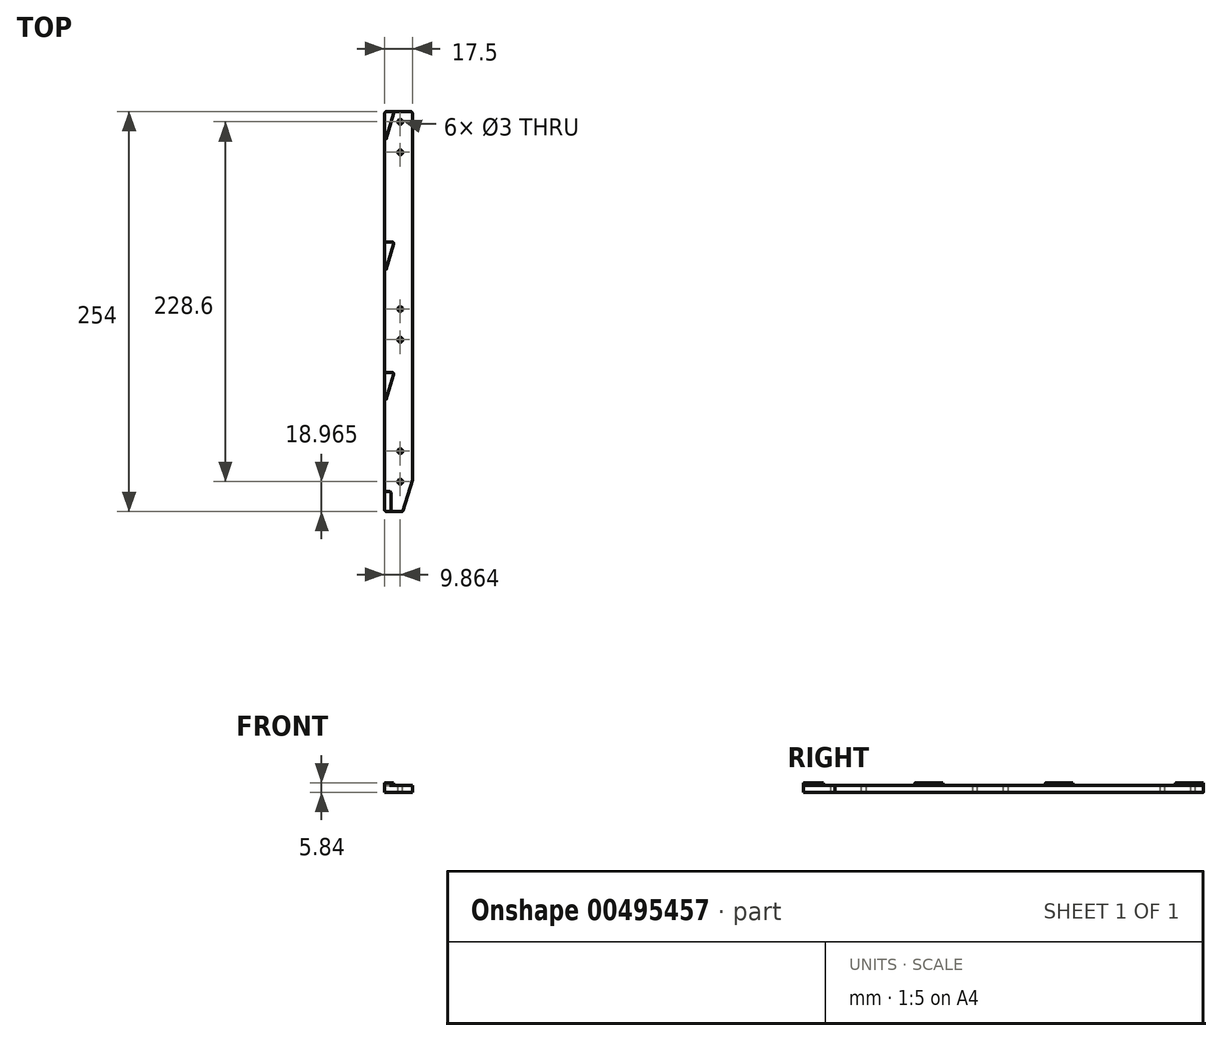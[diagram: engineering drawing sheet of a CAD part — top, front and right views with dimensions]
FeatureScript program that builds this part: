
annotation { "Feature Type Name" : "Feature", "Feature Type Description" : "" }
export const myFeature = defineFeature(function(context is Context, id is Id, definition is map)
    precondition{}
    {
        {
            var Q0;
            Q0=qCreatedBy(makeId("Top.planeOp"),FACE);
            var sketch = newSketch(context, id + "F0", { "sketchPlane" : qUnion([Q0])});
            skLineSegment(sketch, "E0.bottom", {"start": v(-8.75, 106.97) * mm, "end": v(8.75, 106.97) * mm});
            skLineSegment(sketch, "E0.top", {"start": v(-8.75, -147.03) * mm, "end": v(2.75, -147.03) * mm});
            skLineSegment(sketch, "E0.left", {"start": v(-8.75, 106.97) * mm, "end": v(-8.75, -147.03) * mm});
            skLineSegment(sketch, "E0.right", {"start": v(8.75, 106.97) * mm, "end": v(8.75, -127.03) * mm});
            skLineSegment(sketch, "E1", {"start": v(-6.3, -147.03) * mm, "end": v(23.25, -147.03) * mm, "construction": true});
            skLineSegment(sketch, "E2", {"start": v(23.25, -147.03) * mm, "end": v(23.25, -146.28) * mm, "construction": true});
            skLineSegment(sketch, "E3", {"start": v(2.75, -147.03) * mm, "end": v(8.75, -127.03) * mm});
            skLineSegment(sketch, "E4", {"start": v(8.75, -127.03) * mm, "end": v(8.75, -150.96) * mm, "construction": true});
            skSolve(sketch);
        }
        {
            var Q0;
            Q0 = qSketchRegion(id + "F0", true);
            extrude(context, id + "F1", {"entities" : qUnion([Q0]), "oppositeDirection" : true, "depth" : 4.25 * mm});
        }
        {
            var Q0;
            Q0=makeQuery(id+"F1.opExtrude","CAP_FACE",FACE,{"disambiguationData":[OSD([sQuery(id+"F0.wireOp",EDGE,"E0.bottom"),sQuery(id+"F0.wireOp",EDGE,"E0.top"),sQuery(id+"F0.wireOp",EDGE,"E0.left"),sQuery(id+"F0.wireOp",EDGE,"E0.right")])],"isStart":true});
            var sketch = newSketch(context, id + "F2", { "sketchPlane" : qUnion([Q0])});
            skLineSegment(sketch, "E5", {"start": v(-8.75, 106.97) * mm, "end": v(-2.75, 106.97) * mm});
            skLineSegment(sketch, "E6", {"start": v(-2.75, 106.97) * mm, "end": v(-8.75, 86.97) * mm});
            skLineSegment(sketch, "E7", {"start": v(-8.75, 86.97) * mm, "end": v(-8.75, 106.97) * mm});
            skLineSegment(sketch, "E8", {"start": v(-8.75, 24.19) * mm, "end": v(-2.75, 24.19) * mm});
            skLineSegment(sketch, "E9", {"start": v(-2.75, 24.19) * mm, "end": v(-8.75, 4.19) * mm});
            skLineSegment(sketch, "E10", {"start": v(-8.75, 4.19) * mm, "end": v(-8.75, 24.19) * mm});
            skLineSegment(sketch, "E11", {"start": v(-8.75, -58.6) * mm, "end": v(-2.75, -58.6) * mm});
            skLineSegment(sketch, "E12", {"start": v(-2.75, -58.6) * mm, "end": v(-8.75, -78.6) * mm});
            skLineSegment(sketch, "E13", {"start": v(-8.75, -78.6) * mm, "end": v(-8.75, -58.6) * mm});
            skLineSegment(sketch, "E14", {"start": v(-8.75, -134.33) * mm, "end": v(-4.75, -134.33) * mm});
            skLineSegment(sketch, "E15", {"start": v(-4.75, -134.33) * mm, "end": v(-4.75, -147.03) * mm});
            skLineSegment(sketch, "E16", {"start": v(-4.75, -147.03) * mm, "end": v(-8.75, -147.03) * mm});
            skLineSegment(sketch, "E17", {"start": v(-8.75, -147.03) * mm, "end": v(-8.75, -134.33) * mm});
            skSolve(sketch);
        }
        {
            var Q0;
            Q0=makeQuery(id+"F2.imprint","IMPRINT",FACE,{"disambiguationData":[TD([[makeQuery(id+"F2.imprint","IMPRINT",EDGE,{"derivedFrom":sQuery(id+"F2.wireOp",EDGE,"E8")}),-1.0]])]});
            var Q1;
            Q1=makeQuery(id+"F2.imprint","IMPRINT",FACE,{"disambiguationData":[TD([[makeQuery(id+"F2.imprint","IMPRINT",EDGE,{"derivedFrom":sQuery(id+"F2.wireOp",EDGE,"E11")}),-1.0]])]});
            var Q2;
            Q2=makeQuery(id+"F2.imprint","IMPRINT",FACE,{"disambiguationData":[TD([[makeQuery(id+"F2.imprint","IMPRINT",EDGE,{"derivedFrom":sQuery(id+"F2.wireOp",EDGE,"E14")}),-1.0]])]});
            var Q3;
            Q3=makeQuery(id+"F2.imprint","IMPRINT",FACE,{"disambiguationData":[TD([[makeQuery(id+"F2.imprint","IMPRINT",EDGE,{"derivedFrom":sQuery(id+"F2.wireOp",EDGE,"E5")}),-1.0]])]});
            extrude(context, id + "F3", {"entities" : qUnion([Q0, Q1, Q2, Q3]), "operationType" : NewBodyOperationType.ADD, "depth" : 1.59 * mm});
        }
        {
            var Q0;
            Q0=makeQuery(id+"F3.opExtrude","SWEPT_EDGE",EDGE,{"disambiguationData":[OSD([sQuery(id+"F2.wireOp",EDGE,"E11"),sQuery(id+"F2.wireOp",EDGE,"E12")])]});
            var Q1;
            Q1=makeQuery(id+"F3.opExtrude","SWEPT_EDGE",EDGE,{"disambiguationData":[OSD([sQuery(id+"F0.wireOp",EDGE,"E0.left"),sQuery(id+"F2.wireOp",EDGE,"E11"),sQuery(id+"F2.wireOp",EDGE,"E13")])]});
            var Q2;
            Q2=makeQuery(id+"F3.opExtrude","SWEPT_EDGE",EDGE,{"disambiguationData":[OSD([sQuery(id+"F2.wireOp",EDGE,"E8"),sQuery(id+"F2.wireOp",EDGE,"E9")])]});
            var Q3;
            Q3=makeQuery(id+"F3.opExtrude","SWEPT_EDGE",EDGE,{"disambiguationData":[OSD([sQuery(id+"F0.wireOp",EDGE,"E0.left"),sQuery(id+"F2.wireOp",EDGE,"E8"),sQuery(id+"F2.wireOp",EDGE,"E10")])]});
            var Q4;
            Q4=makeQuery(id+"F3.opExtrude","SWEPT_EDGE",EDGE,{"disambiguationData":[OSD([sQuery(id+"F0.wireOp",EDGE,"E0.bottom"),sQuery(id+"F2.wireOp",EDGE,"E5"),sQuery(id+"F2.wireOp",EDGE,"E6")])]});
            var Q5;
            Q5=makeQuery(id+"F3.boolean.opBoolean","MERGE",EDGE,{"derivedFrom":[makeQuery(id+"F1.opExtrude","SWEPT_EDGE",EDGE,{"disambiguationData":[OSD([sQuery(id+"F0.wireOp",EDGE,"E0.bottom"),sQuery(id+"F0.wireOp",EDGE,"E0.left")])]}),makeQuery(id+"F3.opExtrude","SWEPT_EDGE",EDGE,{"disambiguationData":[OSD([sQuery(id+"F2.wireOp",EDGE,"E5"),sQuery(id+"F2.wireOp",EDGE,"E7")])]})]});
            var Q6;
            Q6=makeQuery(id+"F1.opExtrude","SWEPT_EDGE",EDGE,{"disambiguationData":[OSD([sQuery(id+"F0.wireOp",EDGE,"E0.bottom"),sQuery(id+"F0.wireOp",EDGE,"E0.right")])]});
            var Q7;
            Q7=makeQuery(id+"F3.boolean.opBoolean","MERGE",EDGE,{"derivedFrom":[makeQuery(id+"F1.opExtrude","SWEPT_EDGE",EDGE,{"disambiguationData":[OSD([sQuery(id+"F0.wireOp",EDGE,"E0.top"),sQuery(id+"F0.wireOp",EDGE,"E0.left")])]}),makeQuery(id+"F3.opExtrude","SWEPT_EDGE",EDGE,{"disambiguationData":[OSD([sQuery(id+"F2.wireOp",EDGE,"E16"),sQuery(id+"F2.wireOp",EDGE,"E17")])]})]});
            var Q8;
            Q8=makeQuery(id+"F3.opExtrude","SWEPT_EDGE",EDGE,{"disambiguationData":[OSD([sQuery(id+"F0.wireOp",EDGE,"E0.top"),sQuery(id+"F2.wireOp",EDGE,"E15"),sQuery(id+"F2.wireOp",EDGE,"E16")])]});
            var Q9;
            Q9=makeQuery(id+"F3.opExtrude","SWEPT_EDGE",EDGE,{"disambiguationData":[OSD([sQuery(id+"F2.wireOp",EDGE,"E14"),sQuery(id+"F2.wireOp",EDGE,"E15")])]});
            var Q10;
            Q10=makeQuery(id+"F3.opExtrude","SWEPT_EDGE",EDGE,{"disambiguationData":[OSD([sQuery(id+"F0.wireOp",EDGE,"E0.left"),sQuery(id+"F2.wireOp",EDGE,"E14"),sQuery(id+"F2.wireOp",EDGE,"E17")])]});
            var Q11;
            Q11=makeQuery(id+"F1.opExtrude","SWEPT_EDGE",EDGE,{"disambiguationData":[OSD([sQuery(id+"F0.wireOp",EDGE,"E0.top"),sQuery(id+"F0.wireOp",EDGE,"0200dc53-b9c6-442b-89c6-0c7980618248")])]});
            fillet(context, id + "F4", {"entities" : qUnion([Q0, Q1, Q2, Q3, Q4, Q5, Q6, Q7, Q8, Q9, Q10, Q11]), "radius" : 1 * mm, "allowEdgeOverflow" : false});
        }
        {
            var Q0;
            Q0=makeQuery(id+"F3.opExtrude","SWEPT_EDGE",EDGE,{"disambiguationData":[OSD([sQuery(id+"F0.wireOp",EDGE,"E0.left"),sQuery(id+"F2.wireOp",EDGE,"E9"),sQuery(id+"F2.wireOp",EDGE,"E10")])]});
            var Q1;
            Q1=makeQuery(id+"F3.opExtrude","SWEPT_EDGE",EDGE,{"disambiguationData":[OSD([sQuery(id+"F0.wireOp",EDGE,"E0.left"),sQuery(id+"F2.wireOp",EDGE,"E12"),sQuery(id+"F2.wireOp",EDGE,"E13")])]});
            var Q2;
            Q2=makeQuery(id+"F3.opExtrude","SWEPT_EDGE",EDGE,{"disambiguationData":[OSD([sQuery(id+"F0.wireOp",EDGE,"E0.left"),sQuery(id+"F2.wireOp",EDGE,"E6"),sQuery(id+"F2.wireOp",EDGE,"E7")])]});
            fillet(context, id + "F5", {"entities" : qUnion([Q0, Q1, Q2]), "radius" : .4 * mm, "tangentPropagation" : true, "allowEdgeOverflow" : false});
        }
        {
            var Q0;
            Q0=makeQuery(id+"F0.imprint","IMPRINT",FACE,{"disambiguationData":[TD([[makeQuery(id+"F0.imprint","IMPRINT",EDGE,{"derivedFrom":sQuery(id+"F0.wireOp",EDGE,"E0.bottom")}),-1.0]])]});
            var sketch = newSketch(context, id + "F6", { "sketchPlane" : qUnion([Q0])});
            skCircle(sketch, "E18", {"center": v(1.11, 100.53) * mm, "radius": 1.5 * mm});
            skCircle(sketch, "E19", {"center": v(1.11, 81.15) * mm, "radius": 1.5 * mm});
            skCircle(sketch, "E20", {"center": v(1.11, -18.42) * mm, "radius": 1.5 * mm});
            skCircle(sketch, "E21", {"center": v(1.11, -37.92) * mm, "radius": 1.5 * mm});
            skCircle(sketch, "E22", {"center": v(1.11, -128.07) * mm, "radius": 1.5 * mm});
            skCircle(sketch, "E23", {"center": v(1.11, -108.68) * mm, "radius": 1.5 * mm});
            skLineSegment(sketch, "E24", {"start": v(-1.11, -135.49) * mm, "end": v(1.11, -128.07) * mm, "construction": true});
            skLineSegment(sketch, "E25", {"start": v(-1.11, -116.1) * mm, "end": v(1.11, -108.68) * mm, "construction": true});
            skLineSegment(sketch, "E26", {"start": v(-1.11, -45.34) * mm, "end": v(1.11, -37.92) * mm, "construction": true});
            skLineSegment(sketch, "E27", {"start": v(-1.11, -25.84) * mm, "end": v(1.11, -18.42) * mm, "construction": true});
            skLineSegment(sketch, "E28", {"start": v(-1.11, 73.73) * mm, "end": v(1.11, 81.15) * mm, "construction": true});
            skLineSegment(sketch, "E29", {"start": v(-1.11, 93.11) * mm, "end": v(1.11, 100.53) * mm});
            skArc(sketch, "E30.0.startCap", {"start": v(1.28, 92.4) * mm, "mid": v(-1.83, 90.72) * mm, "end": v(-3.5, 93.83) * mm});
            skArc(sketch, "E30.0.endCap", {"start": v(-1.28, 101.25) * mm, "mid": v(1.83, 102.93) * mm, "end": v(3.5, 99.82) * mm});
            skLineSegment(sketch, "E30.0.left", {"start": v(-3.5, 93.83) * mm, "end": v(-1.28, 101.25) * mm});
            skLineSegment(sketch, "E30.0.right", {"start": v(1.28, 92.4) * mm, "end": v(3.5, 99.82) * mm});
            skArc(sketch, "E31.0.startCap", {"start": v(1.28, -136.2) * mm, "mid": v(-1.83, -137.88) * mm, "end": v(-3.5, -134.77) * mm});
            skArc(sketch, "E31.0.endCap", {"start": v(-1.28, -127.35) * mm, "mid": v(1.83, -125.67) * mm, "end": v(3.5, -128.78) * mm});
            skLineSegment(sketch, "E31.0.left", {"start": v(-3.5, -134.77) * mm, "end": v(-1.28, -127.35) * mm});
            skLineSegment(sketch, "E31.0.right", {"start": v(1.28, -136.2) * mm, "end": v(3.5, -128.78) * mm});
            skArc(sketch, "E31.1.startCap", {"start": v(1.28, -116.82) * mm, "mid": v(-1.83, -118.5) * mm, "end": v(-3.5, -115.39) * mm});
            skArc(sketch, "E31.1.endCap", {"start": v(-1.28, -107.96) * mm, "mid": v(1.83, -106.29) * mm, "end": v(3.5, -109.4) * mm});
            skLineSegment(sketch, "E31.1.left", {"start": v(-3.5, -115.39) * mm, "end": v(-1.28, -107.96) * mm});
            skLineSegment(sketch, "E31.1.right", {"start": v(1.28, -116.82) * mm, "end": v(3.5, -109.4) * mm});
            skArc(sketch, "E32.0.startCap", {"start": v(1.28, -46.06) * mm, "mid": v(-1.83, -47.74) * mm, "end": v(-3.5, -44.63) * mm});
            skArc(sketch, "E32.0.endCap", {"start": v(-1.28, -37.2) * mm, "mid": v(1.83, -35.53) * mm, "end": v(3.5, -38.64) * mm});
            skLineSegment(sketch, "E32.0.left", {"start": v(-3.5, -44.63) * mm, "end": v(-1.28, -37.2) * mm});
            skLineSegment(sketch, "E32.0.right", {"start": v(1.28, -46.06) * mm, "end": v(3.5, -38.64) * mm});
            skArc(sketch, "E32.1.startCap", {"start": v(1.28, -26.56) * mm, "mid": v(-1.83, -28.24) * mm, "end": v(-3.5, -25.13) * mm});
            skArc(sketch, "E32.1.endCap", {"start": v(-1.28, -17.7) * mm, "mid": v(1.83, -16.03) * mm, "end": v(3.5, -19.14) * mm});
            skLineSegment(sketch, "E32.1.left", {"start": v(-3.5, -25.13) * mm, "end": v(-1.28, -17.7) * mm});
            skLineSegment(sketch, "E32.1.right", {"start": v(1.28, -26.56) * mm, "end": v(3.5, -19.14) * mm});
            skArc(sketch, "E33.0.startCap", {"start": v(0.32, 73.3) * mm, "mid": v(-1.54, 72.3) * mm, "end": v(-2.55, 74.16) * mm});
            skArc(sketch, "E33.0.endCap", {"start": v(-0.32, 81.58) * mm, "mid": v(1.54, 82.59) * mm, "end": v(2.55, 80.72) * mm});
            skLineSegment(sketch, "E33.0.left", {"start": v(-2.55, 74.16) * mm, "end": v(-0.32, 81.58) * mm});
            skLineSegment(sketch, "E33.0.right", {"start": v(0.32, 73.3) * mm, "end": v(2.55, 80.72) * mm});
            skArc(sketch, "E34.0.startCap", {"start": v(0.32, -135.92) * mm, "mid": v(-1.54, -136.93) * mm, "end": v(-2.55, -135.06) * mm});
            skArc(sketch, "E34.0.endCap", {"start": v(-0.32, -127.63) * mm, "mid": v(1.54, -126.63) * mm, "end": v(2.55, -128.5) * mm});
            skLineSegment(sketch, "E34.0.left", {"start": v(-2.55, -135.06) * mm, "end": v(-0.32, -127.63) * mm});
            skLineSegment(sketch, "E34.0.right", {"start": v(0.32, -135.92) * mm, "end": v(2.55, -128.5) * mm});
            skArc(sketch, "E35.0.startCap", {"start": v(0.32, -116.54) * mm, "mid": v(-1.54, -117.54) * mm, "end": v(-2.55, -115.67) * mm});
            skArc(sketch, "E35.0.endCap", {"start": v(-0.32, -108.25) * mm, "mid": v(1.54, -107.24) * mm, "end": v(2.55, -109.11) * mm});
            skLineSegment(sketch, "E35.0.left", {"start": v(-2.55, -115.67) * mm, "end": v(-0.32, -108.25) * mm});
            skLineSegment(sketch, "E35.0.right", {"start": v(0.32, -116.54) * mm, "end": v(2.55, -109.11) * mm});
            skArc(sketch, "E36.0.startCap", {"start": v(0.32, -45.78) * mm, "mid": v(-1.54, -46.78) * mm, "end": v(-2.55, -44.91) * mm});
            skArc(sketch, "E36.0.endCap", {"start": v(-0.32, -37.49) * mm, "mid": v(1.54, -36.48) * mm, "end": v(2.55, -38.35) * mm});
            skLineSegment(sketch, "E36.0.left", {"start": v(-2.55, -44.91) * mm, "end": v(-0.32, -37.49) * mm});
            skLineSegment(sketch, "E36.0.right", {"start": v(0.32, -45.78) * mm, "end": v(2.55, -38.35) * mm});
            skArc(sketch, "E36.1.startCap", {"start": v(0.32, -26.28) * mm, "mid": v(-1.54, -27.28) * mm, "end": v(-2.55, -25.41) * mm});
            skArc(sketch, "E36.1.endCap", {"start": v(-0.32, -17.99) * mm, "mid": v(1.54, -16.98) * mm, "end": v(2.55, -18.85) * mm});
            skLineSegment(sketch, "E36.1.left", {"start": v(-2.55, -25.41) * mm, "end": v(-0.32, -17.99) * mm});
            skLineSegment(sketch, "E36.1.right", {"start": v(0.32, -26.28) * mm, "end": v(2.55, -18.85) * mm});
            skArc(sketch, "E36.3.startCap", {"start": v(0.32, 92.68) * mm, "mid": v(-1.54, 91.67) * mm, "end": v(-2.55, 93.54) * mm});
            skArc(sketch, "E36.3.endCap", {"start": v(-0.32, 100.97) * mm, "mid": v(1.54, 101.97) * mm, "end": v(2.55, 100.1) * mm});
            skLineSegment(sketch, "E36.3.left", {"start": v(-2.55, 93.54) * mm, "end": v(-0.32, 100.97) * mm});
            skLineSegment(sketch, "E36.3.right", {"start": v(0.32, 92.68) * mm, "end": v(2.55, 100.1) * mm});
            skArc(sketch, "E37.0.startCap", {"start": v(1.28, 73) * mm, "mid": v(-1.83, 71.33) * mm, "end": v(-3.5, 74.45) * mm});
            skArc(sketch, "E37.0.endCap", {"start": v(-1.28, 81.87) * mm, "mid": v(1.83, 83.55) * mm, "end": v(3.5, 80.43) * mm});
            skLineSegment(sketch, "E37.0.left", {"start": v(-3.5, 74.45) * mm, "end": v(-1.28, 81.87) * mm});
            skLineSegment(sketch, "E37.0.right", {"start": v(1.28, 73) * mm, "end": v(3.5, 80.43) * mm});
            skLineSegment(sketch, "E38", {"start": v(0, 107.67) * mm, "end": v(0, -146.33) * mm, "construction": true});
            skSolve(sketch);
        }
        {
            var Q0;
            Q0=sQuery(id+"F6.wireOp",VERTEX,"E29.end");
            var Q1;
            Q1=sQuery(id+"F6.wireOp",VERTEX,"E28.end");
            var Q2;
            Q2=sQuery(id+"F6.wireOp",VERTEX,"E27.end");
            var Q3;
            Q3=sQuery(id+"F6.wireOp",VERTEX,"E26.end");
            var Q4;
            Q4=sQuery(id+"F6.wireOp",VERTEX,"E25.end");
            var Q5;
            Q5=sQuery(id+"F6.wireOp",VERTEX,"E24.end");
            var Q6;
            Q6=makeQuery(id+"F1.opExtrude","SWEPT_BODY",BODY,{"disambiguationData":[OSD([sQuery(id+"F0.wireOp",EDGE,"E0.bottom"),sQuery(id+"F0.wireOp",EDGE,"E0.top"),sQuery(id+"F0.wireOp",EDGE,"E0.left"),sQuery(id+"F0.wireOp",EDGE,"E0.right"),sQuery(id+"F0.wireOp",EDGE,"0200dc53-b9c6-442b-89c6-0c7980618248")])]});
            hole(context, id + "F7", {"style" : HoleStyle.SIMPLE, "endStyle" : HoleEndStyle.THROUGH, "holeDiameter" : 3 * mm, "isTappedThrough" : true, "tappedDepth" : 12 * mm, "tapClearance" : 3, "locations" : qUnion([Q0, Q1, Q2, Q3, Q4, Q5]), "scope" : qUnion([Q6])});
        }
    });
